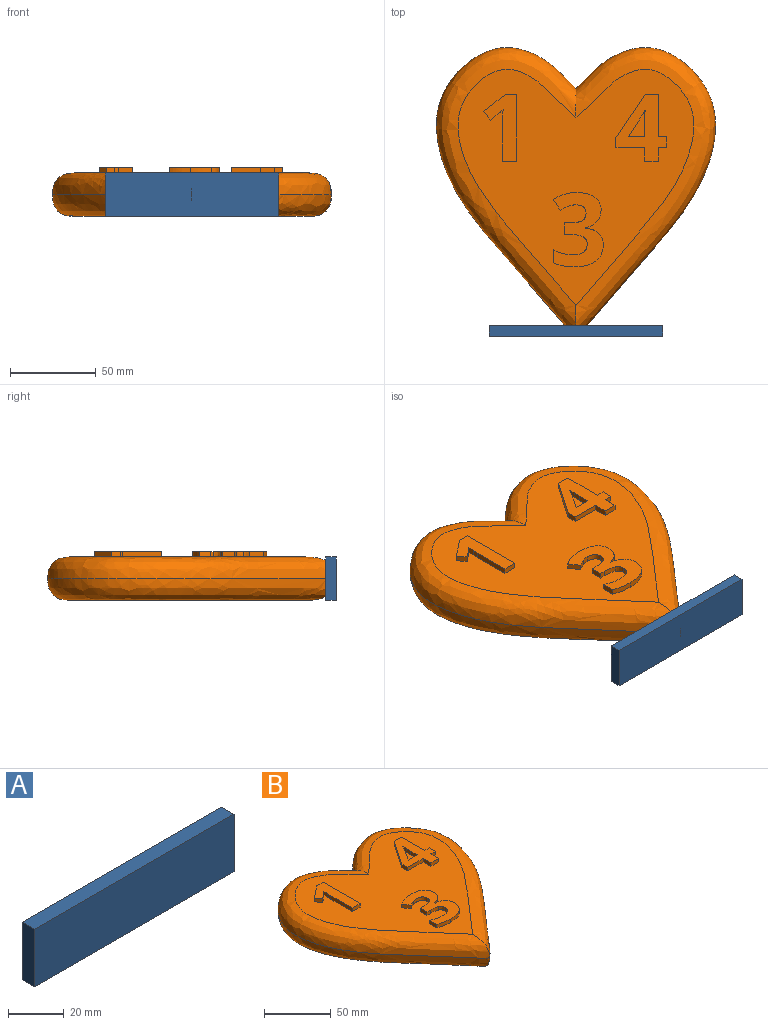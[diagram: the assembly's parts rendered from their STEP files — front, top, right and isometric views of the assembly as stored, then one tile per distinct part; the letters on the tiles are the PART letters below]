
ASSEMBLY  parts=2 mates=1
PART A: 6 faces, bbox 101.6x6.4x25.4 mm
  f0: plane 101.6x6.35mm, normal (0,0,1), area 645.2mm2, adj f1,f3,f4,f5
  f1: plane 25.4x6.35mm, normal (-1,0,0), area 161.3mm2, adj f0,f2,f4,f5
  f2: plane 101.6x6.35mm, normal (0,0,-1), area 645.2mm2, adj f1,f3,f4,f5
  f3: plane 25.4x6.35mm, normal (1,0,0), area 161.3mm2, adj f0,f2,f4,f5
  f4: plane 101.6x25.4mm, normal (0,1,0), area 2580.6mm2, adj f0,f1,f2,f3
  f5: plane 101.6x25.4mm, normal (0,-1,0), area 2580.6mm2, adj f0,f1,f2,f3
PART B: 65 faces, bbox 165.9x171.2x31.1 mm
  f0: plane 140.54x140.52mm, normal (0,0,1), area 10283.9mm2, adj f2,f3,f6,f7,f8,f9,f10,f11
  f1: plane 140.54x140.52mm, normal (0,0,-1), area 12001mm2, adj f4,f5
  f2: bspline ~168.7x99.06mm, area 5187.9mm2, adj f0,f3,f4
  f3: bspline ~168.7x99.06mm, area 5191.1mm2, adj f0,f2,f5
  f4: bspline ~168.7x99.06mm, area 5191.1mm2, adj f1,f2,f5
  f5: bspline ~168.7x99.06mm, area 5187.9mm2, adj f1,f3,f4
  f6: plane 8.26x3.18mm, normal (0,-1,0), area 26.2mm2, adj f0,f7,f15,f16
  f7: plane 39.08x3.18mm, normal (1,0,0), area 124.1mm2, adj f0,f6,f8,f16
  f8: plane 6.79x3.18mm, normal (0,1,0), area 21.6mm2, adj f0,f7,f9,f16
  f9: plane 12.59x10.03mm, normal (-0.62,0.78,0), area 51.1mm2, adj f0,f8,f10,f16
  f10: plane 4.97x3.99mm, normal (-0.78,-0.63,0), area 20.2mm2, adj f0,f9,f11,f16
  f11: plane 4.49x3.61mm, normal (0.63,-0.78,0), area 18.3mm2, adj f0,f10,f12,f16
  f12: extruded ~3.18x2.86mm, area 12.5mm2, adj f0,f11,f13,f16
  f13: plane 4.06x3.18mm, normal (-1,0.03,0), area 12.9mm2, adj f0,f12,f14,f16
  f14: plane 3.71x3.18mm, normal (-1,0.02,0), area 11.8mm2, adj f0,f13,f15,f16
  f15: plane 22.62x3.18mm, normal (-1,0,0), area 71.8mm2, adj f0,f6,f14,f16
  f16: plane 39.08x19.38mm, normal (0,0,1), area 395.1mm2, adj f6,f7,f8,f9,f10,f11,f12,f13
  f17: plane 6.63x3.18mm, normal (-1,0,0), area 21mm2, adj f18,f34,f35,f36
  f18: plane 9.41x3.18mm, normal (0,1,0), area 29.9mm2, adj f17,f19,f35,f36
  f19: plane 10.83x7.17mm, normal (0.83,-0.55,0), area 41.2mm2, adj f18,f20,f35,f36
  f20: extruded ~4.28x3.18mm, area 15.6mm2, adj f19,f21,f35,f36
  f21: plane 3.18x0.21mm, normal (0,-1,0), area 0.7mm2, adj f20,f22,f35,f36
  f22: extruded ~3.67x3.18mm, area 11.7mm2, adj f21,f34,f35,f36
  f23: plane 4.71x3.18mm, normal (0,-1,0), area 14.9mm2, adj f0,f24,f33,f35
  f24: plane 6.42x3.18mm, normal (1,0,0), area 20.4mm2, adj f0,f23,f25,f35
  f25: plane 4.71x3.18mm, normal (0,1,0), area 14.9mm2, adj f0,f24,f26,f35
  f26: plane 24.57x3.18mm, normal (1,0,0), area 78mm2, adj f0,f25,f27,f35
  f27: plane 7.61x3.18mm, normal (0,1,0), area 24.2mm2, adj f0,f26,f28,f35
  f28: plane 25.24x17.14mm, normal (-0.83,0.56,0), area 96.9mm2, adj f0,f27,f29,f35
  f29: plane 5.75x3.18mm, normal (-1,0,0), area 18.3mm2, adj f0,f28,f30,f35
  f30: plane 16.68x3.18mm, normal (0,-1,0), area 53mm2, adj f0,f29,f31,f35
  f31: plane 8.1x3.18mm, normal (-1,0,0), area 25.7mm2, adj f0,f30,f32,f35
  f32: plane 8.08x3.18mm, normal (0,-1,0), area 25.6mm2, adj f0,f31,f33,f35
  f33: plane 8.1x3.18mm, normal (1,0,0), area 25.7mm2, adj f0,f23,f32,f35
  f34: extruded ~4.81x3.18mm, area 15.3mm2, adj f17,f22,f35,f36
  f35: plane 39.08x29.46mm, normal (0,0,1), area 578mm2, adj f17,f18,f19,f20,f21,f22,f23,f24
  f36: plane 15.11x9.76mm, normal (0,0,1), area 68.3mm2, adj f17,f18,f19,f20,f21,f22,f34
  f37: extruded ~6.74x3.18mm, area 23.2mm2, adj f0,f38,f63,f64
  f38: extruded ~7.4x3.8mm, area 27.6mm2, adj f0,f37,f39,f64
  f39: extruded ~10.36x3.18mm, area 34.5mm2, adj f0,f38,f40,f64
  f40: extruded ~13.8x4.16mm, area 46.5mm2, adj f0,f39,f41,f64
  f41: plane 6.15x4.14mm, normal (-0.83,-0.56,0), area 23.5mm2, adj f0,f40,f42,f64
  f42: extruded ~4.78x3.18mm, area 17mm2, adj f0,f41,f43,f64
  f43: extruded ~4.24x3.18mm, area 13.7mm2, adj f0,f42,f44,f64
  f44: extruded ~6.01x4.8mm, area 27.9mm2, adj f0,f43,f45,f64
  f45: extruded ~4.4x3.18mm, area 16.6mm2, adj f0,f44,f46,f64
  f46: extruded ~7.19x3.18mm, area 23.4mm2, adj f0,f45,f47,f64
  f47: plane 3.27x3.18mm, normal (0,1,0), area 10.4mm2, adj f0,f46,f48,f64
  f48: plane 6.86x3.18mm, normal (-1,0,0), area 21.8mm2, adj f0,f47,f49,f64
  f49: plane 3.21x3.18mm, normal (0,-1,0), area 10.2mm2, adj f0,f48,f50,f64
  f50: extruded ~7.75x3.18mm, area 25.1mm2, adj f0,f49,f51,f64
  f51: extruded ~4.21x3.18mm, area 16.4mm2, adj f0,f50,f52,f64
  f52: extruded ~4.83x3.18mm, area 17.4mm2, adj f0,f51,f53,f64
  f53: extruded ~6.54x3.18mm, area 21.6mm2, adj f0,f52,f54,f64
  f54: extruded ~5.84x3.18mm, area 18.8mm2, adj f0,f53,f55,f64
  f55: extruded ~5.4x3.18mm, area 18.4mm2, adj f0,f54,f56,f64
  f56: plane 7.61x3.18mm, normal (-1,0,0), area 24.1mm2, adj f0,f55,f57,f64
  f57: extruded ~12.2x3.18mm, area 39.7mm2, adj f0,f56,f58,f64
  f58: extruded ~12.63x3.4mm, area 42.3mm2, adj f0,f57,f59,f64
  f59: extruded ~9.5x4.42mm, area 34.6mm2, adj f0,f58,f60,f64
  f60: extruded ~6.67x3.18mm, area 23.4mm2, adj f0,f59,f61,f64
  f61: extruded ~7.75x3.18mm, area 27mm2, adj f0,f60,f62,f64
  f62: plane 3.18x0.17mm, normal (1,0,0), area 0.5mm2, adj f0,f61,f63,f64
  f63: extruded ~6.74x3.82mm, area 25mm2, adj f0,f37,f62,f64
  f64: plane 43.46x29.26mm, normal (0,0,1), area 675.7mm2, adj f37,f38,f39,f40,f41,f42,f43,f44
PLACE A t=(-7,-102.27,-12.7)mm
PLACE B at identity
MATE fastened A.f0 <-> B.f0  axis (0,0,1) through (0,-99.1,12.7)mm
